FCSTD DOCUMENT  (FreeCAD 0.21R33771 (Git))
Label: Cutting
License: All rights reserved
LicenseURL: http://en.wikipedia.org/wiki/All_rights_reserved
objects: Part::Part2DObjectPython×17, PartDesign::SubShapeBinder×8
note: 25 computed .brp shape members not serialized (recipe doc carries the construction recipe); baked Part::Feature solids carry a one-line shape summary decoded from their .brp
EXTERNAL_REF file=Upper Plate.FCStd obj=Body004
EXTERNAL_REF file=Connector Plate.FCStd obj=Body
EXTERNAL_REF file=Motor Plate.FCStd obj=Body
EXTERNAL_REF file=Anchor Plate.FCStd obj=Body
EXTERNAL_REF file=Azi Plate.FCStd obj=Body
EXTERNAL_REF file=Alt Plate.FCStd obj=Body
EXTERNAL_REF file=Tripod Pad.FCStd obj=Body
EXTERNAL_REF file=Alt Plate Center.FCStd obj=Body

FEATURE [PartDesign::SubShapeBinder] Binder  label="Upper Plate"
  BindCopyOnChange = 0
  BindMode = 0
  ClaimChildren = false
  Fuse = false
  MakeFace = true
  OffsetFill = false
  OffsetIntersection = false
  OffsetJoinType = 0
  OffsetOpenResult = false
  PartialLoad = false
  Relative = true
  Support = -> [<external Upper Plate.FCStd>#Body004[Pad.]]
  _Version = 2
FEATURE [PartDesign::SubShapeBinder] Binder001  label="Connector Plate"
  BindCopyOnChange = 0
  BindMode = 0
  ClaimChildren = false
  Fuse = false
  MakeFace = true
  OffsetFill = false
  OffsetIntersection = false
  OffsetJoinType = 0
  OffsetOpenResult = false
  PartialLoad = false
  Relative = true
  Support = -> [<external Connector Plate.FCStd>#Body[Pad.]]
  _Version = 2
FEATURE [PartDesign::SubShapeBinder] Binder002  label="Motor Plate"
  BindCopyOnChange = 0
  BindMode = 0
  ClaimChildren = false
  Fuse = false
  MakeFace = true
  OffsetFill = false
  OffsetIntersection = false
  OffsetJoinType = 0
  OffsetOpenResult = false
  PartialLoad = false
  Relative = true
  Support = -> [<external Motor Plate.FCStd>#Body[Pad.]]
  _Version = 2
FEATURE [Part::Part2DObjectPython] Shape2DView  label="Upper Plate View"  # Draft 2D object (typed FeaturePython)
  AutoUpdate = true
  Base = -> Binder
  Clip = false
  FaceNumbers = [52]
  FuseArch = false
  HiddenLines = false
  InPlace = true
  OnlySolids = false
  Projection = (0,8.74228e-08,-1)
  ProjectionMode = 0
  SegmentLength = 0.05
  Tessellation = false
  VisibleOnly = false
FEATURE [Part::Part2DObjectPython] Shape2DView002  label="Connector Plate View"  # Draft 2D object (typed FeaturePython)
  AutoUpdate = true
  Base = -> Binder001
  Clip = false
  FuseArch = false
  HiddenLines = false
  InPlace = true
  OnlySolids = false
  Placement = pos=(80,38,0) rot=(0,0,1;1.5708rad)
  Projection = (0,8.74228e-08,-1)
  ProjectionMode = 0
  SegmentLength = 0.05
  Tessellation = false
  VisibleOnly = false
FEATURE [Part::Part2DObjectPython] Shape2DView003  label="Motor Plate View"  # Draft 2D object (typed FeaturePython)
  AutoUpdate = true
  Base = -> Binder002
  Clip = false
  FuseArch = false
  HiddenLines = false
  InPlace = true
  OnlySolids = false
  Placement = pos=(134,7,0) rot=(0,0,1;0rad)
  Projection = (-1,1.19209e-07,1.68587e-07)
  ProjectionMode = 0
  SegmentLength = 0.05
  Tessellation = false
  VisibleOnly = false
FEATURE [Part::Part2DObjectPython] Shape2DView004  label="Connector Plate View001"  # Draft 2D object (typed FeaturePython)
  AutoUpdate = true
  Base = -> Binder001
  Clip = false
  FuseArch = false
  HiddenLines = false
  InPlace = true
  OnlySolids = false
  Placement = pos=(-38,42,0) rot=(0,0,1;1.5708rad)
  Projection = (0,8.74228e-08,-1)
  ProjectionMode = 0
  SegmentLength = 0.05
  Tessellation = false
  VisibleOnly = false
FEATURE [Part::Part2DObjectPython] Shape2DView005  label="Motor Plate View001"  # Draft 2D object (typed FeaturePython)
  AutoUpdate = true
  Base = -> Binder002
  Clip = false
  FuseArch = false
  HiddenLines = false
  InPlace = true
  OnlySolids = false
  Placement = pos=(-83,-103,0) rot=(0,0,1;3.14159rad)
  Projection = (-1,-1.42e-14,2.38419e-07)
  ProjectionMode = 0
  SegmentLength = 0.05
  Tessellation = false
  VisibleOnly = false
FEATURE [Part::Part2DObjectPython] Rectangle  # Draft 2D object (typed FeaturePython)
  Area = 42828.9
  ChamferSize = 0
  Columns = 1
  FilletRadius = 0
  Height = 180.34
  Length = 237.49
  MakeFace = true
  Placement = pos=(-100.053,-115.98,11) rot=(0,0,1;0rad)
  Rows = 1
FEATURE [PartDesign::SubShapeBinder] Binder003  label="Anchor Plate"
  BindCopyOnChange = 0
  BindMode = 0
  ClaimChildren = false
  Fuse = false
  MakeFace = true
  OffsetFill = false
  OffsetIntersection = false
  OffsetJoinType = 0
  OffsetOpenResult = false
  PartialLoad = false
  Relative = true
  Support = -> [<external Anchor Plate.FCStd>#Body[Hole001.Face2]]
  _Version = 2
FEATURE [PartDesign::SubShapeBinder] Binder004  label="Azi Plate"
  BindCopyOnChange = 0
  BindMode = 0
  ClaimChildren = false
  Fuse = false
  MakeFace = true
  OffsetFill = false
  OffsetIntersection = false
  OffsetJoinType = 0
  OffsetOpenResult = false
  PartialLoad = false
  Relative = true
  Support = -> [<external Azi Plate.FCStd>#Body[Hole.Face2]]
  _Version = 2
FEATURE [PartDesign::SubShapeBinder] Binder005  label="Alt Plate"
  BindCopyOnChange = 0
  BindMode = 0
  ClaimChildren = false
  Fuse = false
  MakeFace = true
  OffsetFill = false
  OffsetIntersection = false
  OffsetJoinType = 0
  OffsetOpenResult = false
  PartialLoad = false
  Placement = pos=(0,0,0) rot=(1,0,0;1.5708rad)
  Relative = true
  Support = -> [<external Alt Plate.FCStd>#Body[Hole.Face4]]
  _Version = 2
FEATURE [Part::Part2DObjectPython] Shape2DView006  label="Anchor Plate View"  # Draft 2D object (typed FeaturePython)
  AutoUpdate = true
  Base = -> Binder003
  Clip = false
  FuseArch = false
  HiddenLines = false
  InPlace = true
  OnlySolids = false
  Placement = pos=(-18.2,179.8,0) rot=(0,0,1;0rad)
  Projection = (0,0,-1)
  ProjectionMode = 0
  SegmentLength = 0.05
  Tessellation = false
  VisibleOnly = false
FEATURE [Part::Part2DObjectPython] Shape2DView007  label="Azi Plate View"  # Draft 2D object (typed FeaturePython)
  AutoUpdate = true
  Base = -> Binder004
  Clip = false
  FuseArch = false
  HiddenLines = false
  InPlace = true
  OnlySolids = false
  Placement = pos=(81.1,140.2,0) rot=(0,0,1;0rad)
  Projection = (0,0,-1)
  ProjectionMode = 0
  SegmentLength = 0.05
  Tessellation = false
  VisibleOnly = false
FEATURE [Part::Part2DObjectPython] Shape2DView008  label="Alt Plate View"  # Draft 2D object (typed FeaturePython)
  AutoUpdate = true
  Base = -> Binder005
  Clip = false
  FuseArch = false
  HiddenLines = false
  InPlace = true
  OnlySolids = false
  Placement = pos=(51.9,216.3,0) rot=(0,0,1;1.5708rad)
  Projection = (0,0,-1)
  ProjectionMode = 0
  SegmentLength = 0.05
  Tessellation = false
  VisibleOnly = false
FEATURE [Part::Part2DObjectPython] Shape2DView009  label="Alt Plate View001"  # Draft 2D object (typed FeaturePython)
  AutoUpdate = true
  Base = -> Binder005
  Clip = false
  FuseArch = false
  HiddenLines = false
  InPlace = true
  OnlySolids = false
  Placement = pos=(10.4,105.5,0) rot=(0,0,-1;1.5708rad)
  Projection = (0,0,-1)
  ProjectionMode = 0
  SegmentLength = 0.05
  Tessellation = false
  VisibleOnly = false
FEATURE [Part::Part2DObjectPython] Rectangle001  # Draft 2D object (typed FeaturePython)
  Area = 30967.7
  ChamferSize = 0
  Columns = 1
  FilletRadius = 0
  Height = 203.2
  Length = 152.4
  MakeFace = true
  Placement = pos=(-69.1632,85.5899,0) rot=(0.707107,0.707107,0;3.14159rad)
  Rows = 1
FEATURE [Part::Part2DObjectPython] Shape2DView010  label="Alt Plate View002"  # Draft 2D object (typed FeaturePython)
  AutoUpdate = true
  Base = -> Binder005
  Clip = false
  FuseArch = false
  HiddenLines = false
  InPlace = true
  OnlySolids = false
  Placement = pos=(0,320.1,0) rot=(0,0,1;0rad)
  Projection = (6.18172e-08,-6.18172e-08,-1)
  ProjectionMode = 0
  SegmentLength = 0.05
  Tessellation = false
  VisibleOnly = false
FEATURE [Part::Part2DObjectPython] Shape2DView011  label="Alt Plate View003"  # Draft 2D object (typed FeaturePython)
  AutoUpdate = true
  Base = -> Binder005
  Clip = false
  FuseArch = false
  HiddenLines = false
  InPlace = true
  OnlySolids = false
  Placement = pos=(-48.7,305.7,0) rot=(0,0,1;3.14159rad)
  Projection = (6.18172e-08,-6.18172e-08,-1)
  ProjectionMode = 0
  SegmentLength = 0.05
  Tessellation = false
  VisibleOnly = false
FEATURE [Part::Part2DObjectPython] Rectangle002  # Draft 2D object (typed FeaturePython)
  Area = 7432.24
  ChamferSize = 0
  Columns = 1
  FilletRadius = 0
  Height = 91.44
  Length = 81.28
  MakeFace = true
  Placement = pos=(-72.0137,272.796,3.09998) rot=(0.707107,0.707107,0;3.14159rad)
  Rows = 1
FEATURE [Part::Part2DObjectPython] Rectangle003  # Draft 2D object (typed FeaturePython)
  Area = 31612.8
  ChamferSize = 0
  Columns = 1
  FilletRadius = 0
  Height = 177.8
  Length = 177.8
  MakeFace = true
  Placement = pos=(39.8965,266.489,0) rot=(0.707107,0.707107,0;3.14159rad)
  Rows = 1
FEATURE [PartDesign::SubShapeBinder] Binder006  label="Tripod Pad"
  BindCopyOnChange = 0
  BindMode = 0
  ClaimChildren = false
  Fuse = false
  MakeFace = true
  OffsetFill = false
  OffsetIntersection = false
  OffsetJoinType = 0
  OffsetOpenResult = false
  PartialLoad = false
  Relative = true
  Support = -> [<external Tripod Pad.FCStd>#Body[Pad.]]
  _Version = 2
FEATURE [Part::Part2DObjectPython] Shape2DView012  label="Tripod Pad View"  # Draft 2D object (typed FeaturePython)
  AutoUpdate = true
  Base = -> Binder006
  Clip = false
  FuseArch = false
  HiddenLines = false
  InPlace = true
  OnlySolids = false
  Placement = pos=(130.4,357.5,0) rot=(0,0,1;0rad)
  Projection = (6.18172e-08,-6.18172e-08,-1)
  ProjectionMode = 0
  SegmentLength = 0.05
  Tessellation = false
  VisibleOnly = false
FEATURE [PartDesign::SubShapeBinder] Binder007  label="Alt Plate Center"
  BindCopyOnChange = 0
  BindMode = 0
  ClaimChildren = false
  Fuse = false
  MakeFace = true
  OffsetFill = false
  OffsetIntersection = false
  OffsetJoinType = 0
  OffsetOpenResult = false
  PartialLoad = false
  Relative = true
  Support = -> [<external Alt Plate Center.FCStd>#Body[Hole.Face4]]
  _Version = 2
FEATURE [Part::Part2DObjectPython] Shape2DView013  label="Alt Plate Center View"  # Draft 2D object (typed FeaturePython)
  AutoUpdate = true
  Base = -> Binder007
  Clip = false
  FuseArch = false
  HiddenLines = false
  InPlace = true
  OnlySolids = false
  Placement = pos=(-21.4,415.2,0) rot=(0,0,1;0rad)
  Projection = (0,-1,0)
  ProjectionMode = 0
  SegmentLength = 0.05
  Tessellation = false
  VisibleOnly = false
